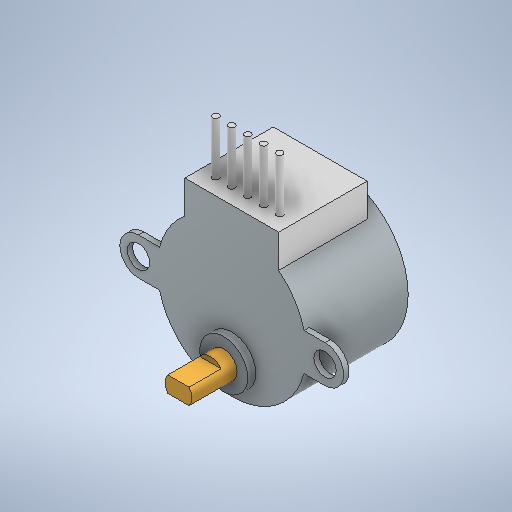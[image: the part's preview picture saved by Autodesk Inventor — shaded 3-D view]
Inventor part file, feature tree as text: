
AUTODESK INVENTOR PART (.ipt)
format: ipt  version: 2025 (Build 290162000, 162)  size: 323,072 bytes
history: native  units: mm
features: extrude x7, sketch x7, other x1, pattern_linear x1
ambient origin geometry x8: Origin, YZ Plane, XZ Plane, XY Plane, X Axis, Y Axis, Z Axis, Center Point
bodies: Body1 (feature_tree)
feature tree (16):
  other  "ソリッド1"
  extrude  "本体"  Depth=28.0mm
  extrude  "タブ"  Depth=19.1mm TaperAngle=0.0deg
  extrude  "押し出し3"  Depth=4.2mm
  extrude  "押し出し4"  Depth=35.0mm
  extrude  "押し出し5"  Depth=7.0mm
  extrude  "押し出し6"  Depth=1.0mm TaperAngle=0.0deg
  extrude  "押し出し7"  Depth=9.0mm
  pattern_linear  "矩形状パターン1"  Spacing1=8.0mm  [1 undecoded]
  sketch  "スケッチ2"
  sketch  "スケッチ3"
  sketch  "スケッチ4"
  sketch  "スケッチ5"
  sketch  "スケッチ6"
  sketch  "スケッチ7"
  sketch  "スケッチ8"
note: 1 required parameter value undecoded (feature->parameter linkage not recoverable at this tier; creation-order binding heuristic only, values carry confidence <= 0.55)
